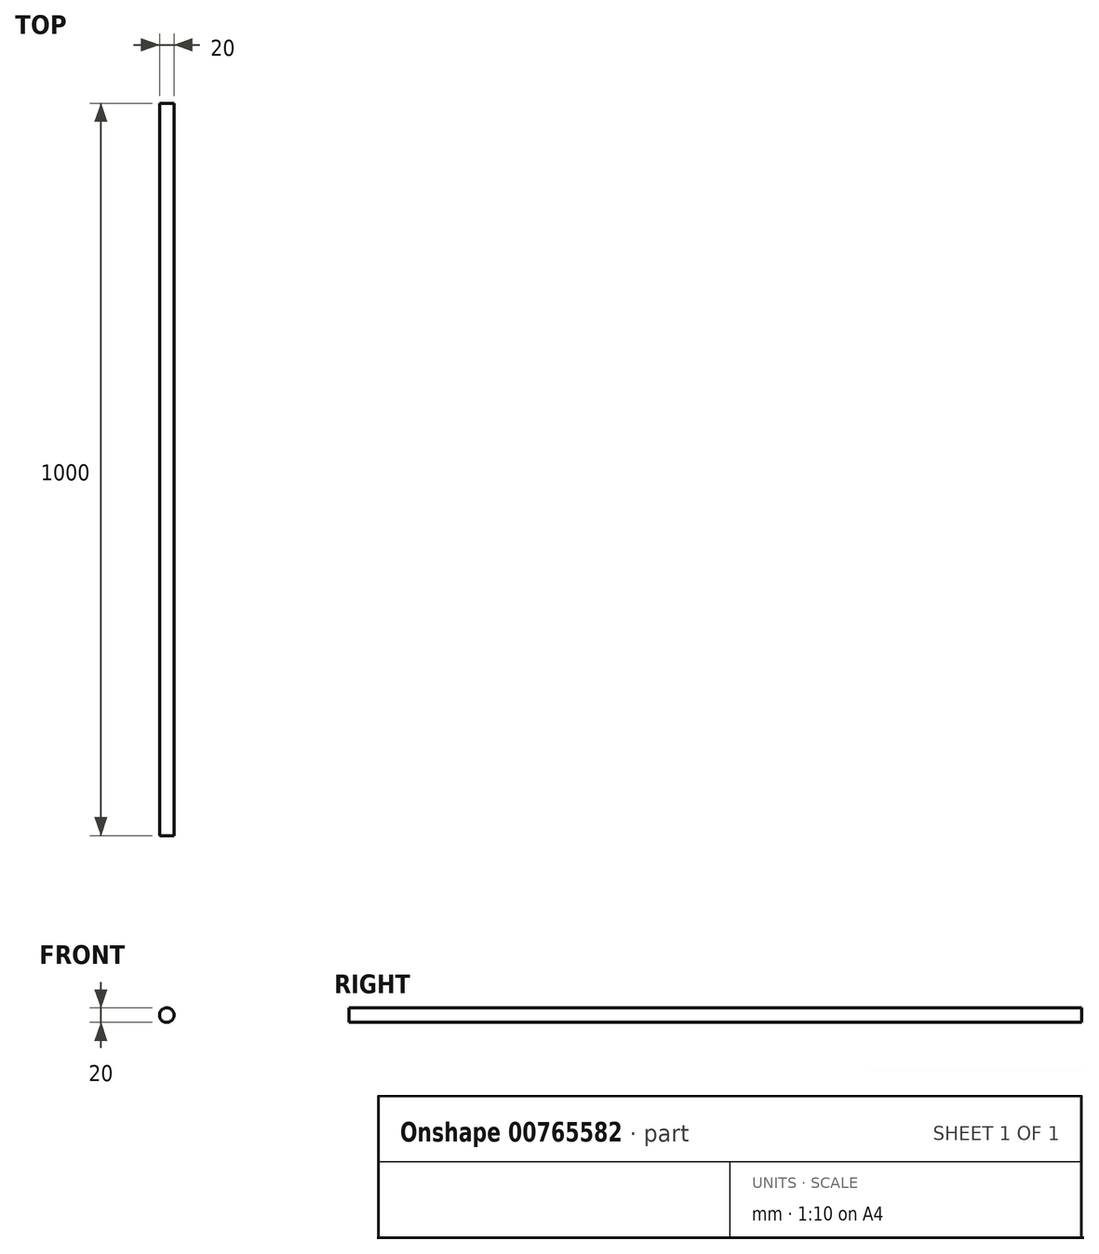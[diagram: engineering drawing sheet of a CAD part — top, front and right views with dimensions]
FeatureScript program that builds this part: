
annotation { "Feature Type Name" : "Feature", "Feature Type Description" : "" }
export const myFeature = defineFeature(function(context is Context, id is Id, definition is map)
    precondition{}
    {
        {
            var Q0;
            Q0=qCreatedBy(makeId("Front.planeOp"),FACE);
            var sketch = newSketch(context, id + "F0", { "sketchPlane" : qUnion([Q0])});
            skCircle(sketch, "E0", {"center": v(0, 0) * mm, "radius": 10 * mm});
            skSolve(sketch);
        }
        {
            var Q0;
            Q0=makeQuery(id+"F0.imprint","IMPRINT",FACE,{"disambiguationData":[TD([[makeQuery(id+"F0.imprint","IMPRINT",EDGE,{"derivedFrom":sQuery(id+"F0.wireOp",EDGE,"E0")}),1.0]])]});
            extrude(context, id + "F1", {"entities" : qUnion([Q0]), "depth" : 1000 * mm, "offsetDistance" : 25 * mm});
        }
    });
